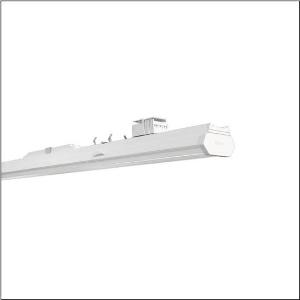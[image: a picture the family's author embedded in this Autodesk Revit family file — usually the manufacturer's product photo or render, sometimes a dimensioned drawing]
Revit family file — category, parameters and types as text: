
# Revit family: licross_11_protected_ho_51tp11dn4f5s
name_source: partatom
category: Lighting Fixtures
units: mm (PartAtom-declared; Revit-internal decimal feet)

## family parameters
Cut with Voids When Loaded = No
Host = Face
Light Source = No
Part Type = Normal
Room Calculation Point = No
Round Connector Dimension = Use Diameter
Shared = No

## types (1)
- --- (1 x LED, 15510 lm, 87.3 W, 4000K)
    Apparent Load = 87 VA
    CIE Flux Codes = 84 94 98 99 100
    Color Rendering = 80
    Color Temperature = 4000K
    Default Elevation = 1800 mm
    Description = Licross 11 Protected HO, luminaire insert, of sheet steel, galvanised, coil coated, white, length: 1.500mm, width: 90mm, height: 101mm, LED rated luminous flux: 15.510lm, light colour: 840, SDCM (Standard Deviation of Colour Matching)MacAdam ≤ 2 SDCM (initial), control gear: DALI 2, with plug, 5-pole, with phase selection, mains connection: 220..240V, AC, 50/60Hz, rated input power: 87W, internal wiring halogen-free, primary light control with lens, of plastic, primary optical cover: cover, of PMMA, light emission: direct distribution, primary light characteristic: symmetric, protection rating (complete): IP64, insulation class (complete): insulation class I (protective earthing), certification: CE, ENEC, VDE, UKCA, protection symbol: D if used in an environment with conductive dust loads with corresponding accessories, impact resistance: IK06, permissible ambient temperature for indoor applications: -25..+30°C, corresponds to IFS (International Featured Standards) requirements for safety and quality in the food industry, reducing of maximum allowable ambient temperature of 5°C with ceiling mounting, LABS conformity tested according to VDMA 24364:2018-05, The light source and the operating device comply with the requirements of the Ecodesign Regulation (EU) 2019/2020 and are replaceable in accordance with this regulation, packaging unit: 1 piece
    Height = 92 mm
    Lamp = 1 x LED
    Lamp Light Flux = 15510 lm
    Lamp Power = 87.3 W
    Lamp count = 1
    Length = 1500 mm
    Luminous efficacy = 178 lm/W
    Manufacturer = Siteco
    ModVariant = No
    Model = 51TP11DN4F5S
    Mounting Place = Ceiling
    Mounting Type = Pendant
    Number of Poles = 1
    OnlyDefault = Yes
    Power Factor = 1
    Product Name = Licross 11 Protected HO
    Product group = luminaire insert | ceiling pendant
    ProductGroupID = 901
    Protection Class = Protection class I
    Protection Degree = IP 64
    RLX_Detail_Level = 1
    RLX_Emergency_Light_Flux = 0 lm
    RLX_Emergency_Type = 0
    RLX_Emergency_Type_DB = No
    RlxData = <blob elided: 24637 chars, md5=35d1d91a>
    Socket = socket
    Standby Power = 0 W
    System Light Flux = 15510 lm
    System Power = 87 W
    Type Comments = factory setting: luminous flux: 100 % | dim-lin: 254 | 589 mA
    Type Image = l_1256148.jpg
    URL = http://relux.com
    VarID = @adj_104155
    Voltage = 0 V
    Weight = 0.00 kg
    Width = 88 mm

## geometry (parser evidence)
native form markers: Blend x4, Sweep x10
no freeform markers — native parametric forms only
